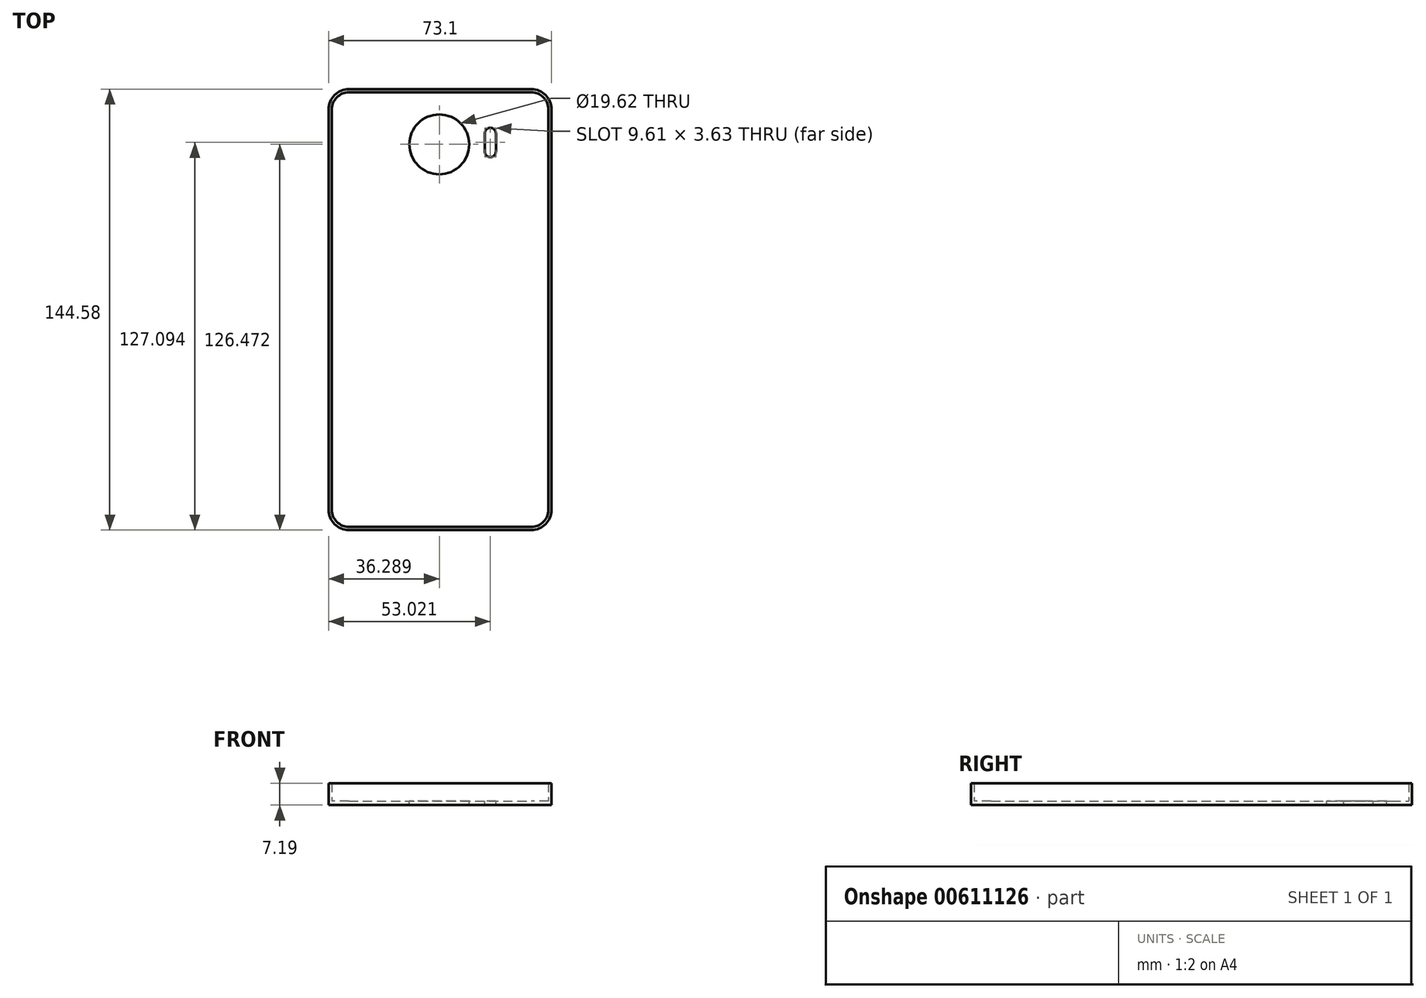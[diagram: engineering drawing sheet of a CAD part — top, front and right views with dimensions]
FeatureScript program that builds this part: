
annotation { "Feature Type Name" : "Feature", "Feature Type Description" : "" }
export const myFeature = defineFeature(function(context is Context, id is Id, definition is map)
    precondition{}
    {
        {
            var Q0;
            Q0=qCreatedBy(makeId("Top.planeOp"),FACE);
            var sketch = newSketch(context, id + "F0", { "sketchPlane" : qUnion([Q0])});
            skLineSegment(sketch, "E0.bottom", {"start": v(5.63, 0) * mm, "end": v(65.4, 0) * mm});
            skLineSegment(sketch, "E0.top", {"start": v(5.63, 142.5) * mm, "end": v(65.4, 142.5) * mm});
            skLineSegment(sketch, "E0.left", {"start": v(0, 5.63) * mm, "end": v(0, 136.87) * mm});
            skLineSegment(sketch, "E0.right", {"start": v(71.02, 5.63) * mm, "end": v(71.02, 136.87) * mm});
            skCircle(sketch, "E1", {"center": v(51.98, 129.04) * mm, "radius": 1.82 * mm});
            skCircle(sketch, "E2", {"center": v(51.98, 123.06) * mm, "radius": 1.82 * mm});
            skLineSegment(sketch, "E3", {"start": v(50.16, 123.06) * mm, "end": v(50.16, 129.04) * mm});
            skLineSegment(sketch, "E4", {"start": v(53.8, 129.04) * mm, "end": v(53.8, 123.06) * mm});
            skCircle(sketch, "E5", {"center": v(35.25, 125.43) * mm, "radius": 9.81 * mm});
            skPoint(sketch, "E6.visualSharp", {"position": v(0, 142.5) * mm});
            skArc(sketch, "E6.filletArc", {"start": v(5.63, 142.5) * mm, "mid": v(1.65, 140.85) * mm, "end": v(0, 136.87) * mm});
            skPoint(sketch, "E7.visualSharp", {"position": v(71.02, 142.5) * mm});
            skArc(sketch, "E7.filletArc", {"start": v(71.02, 136.87) * mm, "mid": v(69.37, 140.85) * mm, "end": v(65.4, 142.5) * mm});
            skPoint(sketch, "E8.visualSharp", {"position": v(71.02, 0) * mm});
            skArc(sketch, "E8.filletArc", {"start": v(65.4, 0) * mm, "mid": v(69.37, 1.65) * mm, "end": v(71.02, 5.63) * mm});
            skPoint(sketch, "E9.visualSharp", {"position": v(0, 0) * mm});
            skArc(sketch, "E9.filletArc", {"start": v(0, 5.63) * mm, "mid": v(1.65, 1.65) * mm, "end": v(5.63, 0) * mm});
            skSolve(sketch);
        }
        {
            var Q0;
            Q0=makeQuery(id+"F0.imprint","IMPRINT",FACE,{"disambiguationData":[TD([[makeQuery(id+"F0.imprint","IMPRINT",EDGE,{"derivedFrom":sQuery(id+"F0.wireOp",EDGE,"E0.bottom")}),1.0]])]});
            extrude(context, id + "F1", {"entities" : qUnion([Q0]), "oppositeDirection" : true, "depth" : 1.3 * mm, "offsetDistance" : 25.4 * mm});
        }
        {
            var Q0;
            Q0=makeQuery(id+"F1.opExtrude","CAP_FACE",FACE,{"disambiguationData":[OSD([sQuery(id+"F0.wireOp",EDGE,"E0.bottom"),sQuery(id+"F0.wireOp",EDGE,"E0.top"),sQuery(id+"F0.wireOp",EDGE,"E0.left"),sQuery(id+"F0.wireOp",EDGE,"E0.right"),sQuery(id+"F0.wireOp",EDGE,"E1"),sQuery(id+"F0.wireOp",EDGE,"E2"),sQuery(id+"F0.wireOp",EDGE,"E3"),sQuery(id+"F0.wireOp",EDGE,"E4"),sQuery(id+"F0.wireOp",EDGE,"E5"),sQuery(id+"F0.wireOp",EDGE,"E6.filletArc"),sQuery(id+"F0.wireOp",EDGE,"E7.filletArc"),sQuery(id+"F0.wireOp",EDGE,"E8.filletArc"),sQuery(id+"F0.wireOp",EDGE,"E9.filletArc")])],"isStart":true});
            var sketch = newSketch(context, id + "F2", { "sketchPlane" : qUnion([Q0])});
            skLineSegment(sketch, "E10", {"start": v(-1.04, 136.87) * mm, "end": v(-1.04, 5.63) * mm});
            skLineSegment(sketch, "E11", {"start": v(5.63, 143.54) * mm, "end": v(65.4, 143.54) * mm});
            skLineSegment(sketch, "E12", {"start": v(5.63, -1.04) * mm, "end": v(65.4, -1.04) * mm});
            skLineSegment(sketch, "E13", {"start": v(72.06, 136.87) * mm, "end": v(72.06, 5.63) * mm});
            skArc(sketch, "E14", {"start": v(5.63, 143.54) * mm, "mid": v(0.91, 141.58) * mm, "end": v(-1.04, 136.87) * mm});
            skArc(sketch, "E15", {"start": v(65.4, 143.54) * mm, "mid": v(70.1, 141.58) * mm, "end": v(72.06, 136.87) * mm});
            skArc(sketch, "E16", {"start": v(72.06, 5.63) * mm, "mid": v(70.1, 0.91) * mm, "end": v(65.4, -1.04) * mm});
            skArc(sketch, "E17", {"start": v(5.63, -1.04) * mm, "mid": v(0.91, 0.91) * mm, "end": v(-1.04, 5.63) * mm});
            skSolve(sketch);
        }
        {
            var Q0;
            Q0=makeQuery(id+"F2.imprint","IMPRINT",FACE,{"disambiguationData":[TD([[makeQuery(id+"F2.imprint","IMPRINT",EDGE,{"derivedFrom":sQuery(id+"F2.wireOp",EDGE,"E10")}),1.0]])]});
            var Q1;
            Q1=makeQuery(id+"F1.opExtrude","CAP_FACE",FACE,{"disambiguationData":[OSD([sQuery(id+"F0.wireOp",EDGE,"E0.bottom"),sQuery(id+"F0.wireOp",EDGE,"E0.top"),sQuery(id+"F0.wireOp",EDGE,"E0.left"),sQuery(id+"F0.wireOp",EDGE,"E0.right"),sQuery(id+"F0.wireOp",EDGE,"E1"),sQuery(id+"F0.wireOp",EDGE,"E2"),sQuery(id+"F0.wireOp",EDGE,"E3"),sQuery(id+"F0.wireOp",EDGE,"E4"),sQuery(id+"F0.wireOp",EDGE,"E5"),sQuery(id+"F0.wireOp",EDGE,"E6.filletArc"),sQuery(id+"F0.wireOp",EDGE,"E7.filletArc"),sQuery(id+"F0.wireOp",EDGE,"E8.filletArc"),sQuery(id+"F0.wireOp",EDGE,"E9.filletArc")])],"isStart":false});
            extrude(context, id + "F3", {"entities" : qUnion([Q0]), "operationType" : NewBodyOperationType.ADD, "depth" : 5.9 * mm, "offsetDistance" : 25.4 * mm, "hasSecondDirection" : true, "secondDirectionBound" : SecondDirectionBoundingType.UP_TO_SURFACE, "secondDirectionOppositeDirection" : true, "secondDirectionDepth" : 25.4 * mm, "secondDirectionBoundEntityFace" : qUnion([Q1])});
        }
    });
